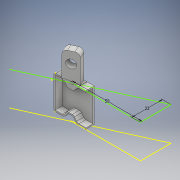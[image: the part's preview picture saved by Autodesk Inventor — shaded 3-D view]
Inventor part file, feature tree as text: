
AUTODESK INVENTOR PART (.ipt)
format: ipt  version: 2017.3 (Build 213256000, 256)  size: 259,072 bytes
history: native  units: mm
features: sketch x7, extrude x3, fillet x3, plane x2, shell x1, hole x1, projected_geometry x1
ambient origin geometry x8: Origin, YZ Plane, XZ Plane, XY Plane, X Axis, Y Axis, Z Axis, Center Point
bodies: Solid1 (feature_tree)
feature tree (18):
  extrude  "Extrusion1"  Depth=4.5mm
  shell  "Shell1"  Thickness=6.0mm
  sketch  "Sketch2"  dims[d9=2.0mm d10=11.0mm]
  sketch  "Sketch3"  dims[d11=11.0mm d12=5.0mm d13=0.0mm d14=1.0mm]
  plane  "Work Plane2"
  sketch  "Sketch4"  dims[d15=50.0mm d17=22.0mm d19=90.0deg d20=10.0mm]
  plane  "Work Plane4"
  extrude  "Extrusion2"  Depth=11.0mm
  extrude  "Extrusion3"  Depth=1.0mm TaperAngle=0.0deg
  fillet  "Fillet1"  Radius=1.0mm
  hole  "Hole1"  [1 undecoded]
  fillet  "Fillet2"  [1 undecoded]
  fillet  "Fillet3"  Radius=10.0mm
  sketch  "Sketch1"  dims[d0=22.0mm d4=4.5mm d7=6.0mm]
  sketch  "Sketch5"  dims[d21=5.0mm]
  sketch  "Sketch6"  dims[d22=20.0mm d23=0.0mm]
  projected_geometry  "Projected Loop1"
  sketch  "Sketch7"  dims[d24=6.0mm d25=0.0mm d26=1.0mm d27=0.0mm d28=3.0mm d29=1.0mm d30=12.0mm d31=6.0mm d32=6.0mm d33=4.0mm d34=2.0mm d35=90.0deg d36=8.0mm d37=20.594885mm d38=10.0mm d39=5.0mm d40=3.0mm d41=1.5mm]
note: 2 required parameter values undecoded (feature->parameter linkage not recoverable at this tier; creation-order binding heuristic only, values carry confidence <= 0.55)
